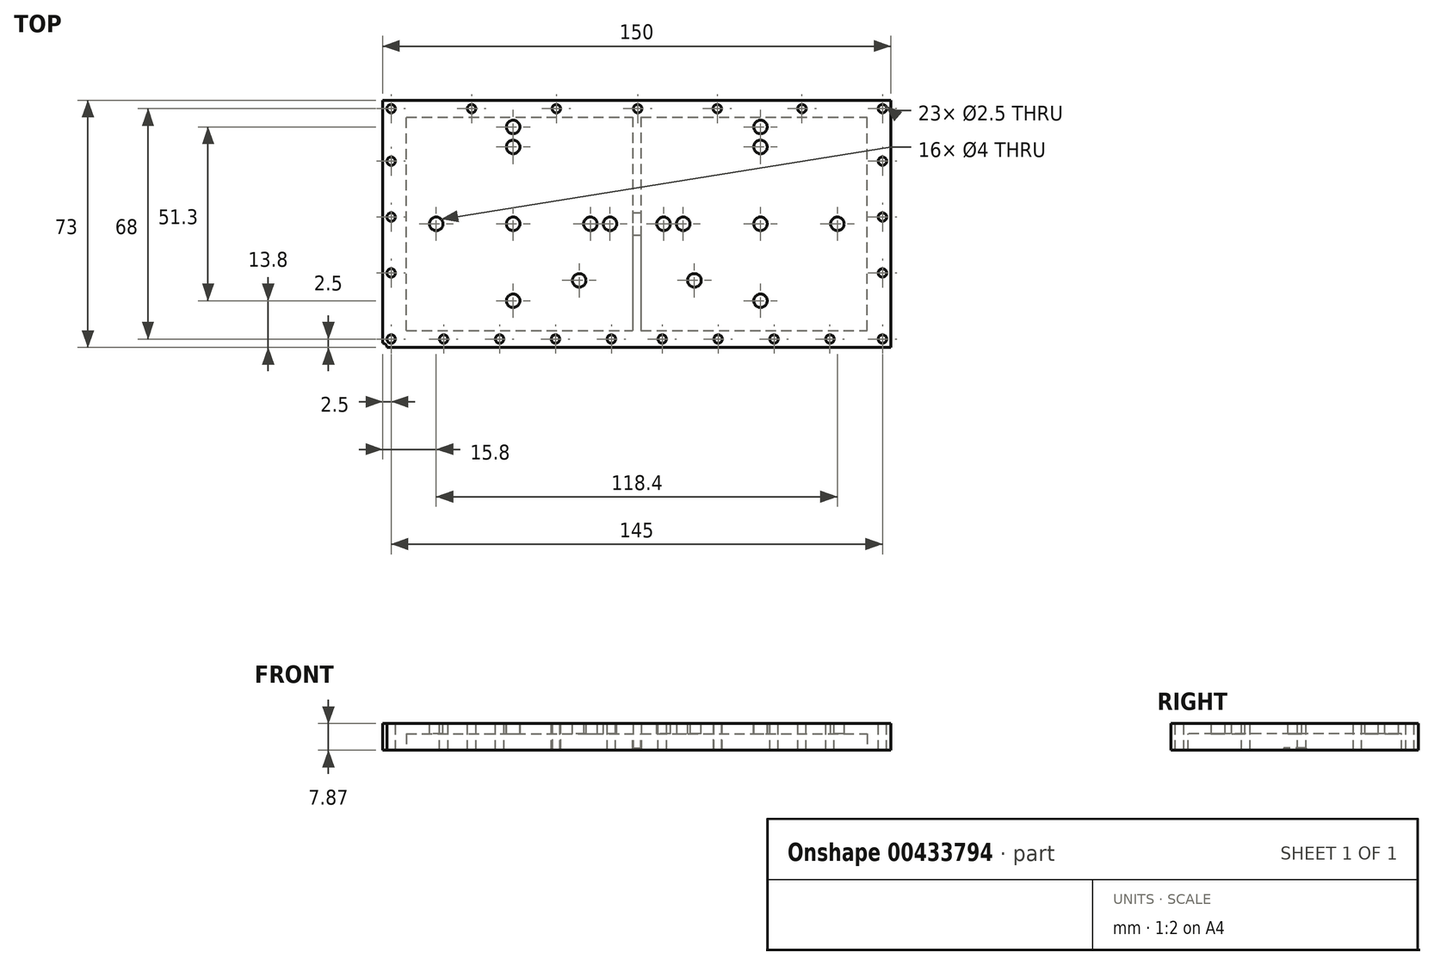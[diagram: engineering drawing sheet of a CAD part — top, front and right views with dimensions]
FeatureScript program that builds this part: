
annotation { "Feature Type Name" : "Feature", "Feature Type Description" : "" }
export const myFeature = defineFeature(function(context is Context, id is Id, definition is map)
    precondition{}
    {
        {
            var Q0;
            Q0=qCreatedBy(makeId("Top.planeOp"),FACE);
            var sketch = newSketch(context, id + "F0", { "sketchPlane" : qUnion([Q0])});
            skLineSegment(sketch, "E0.bottom", {"start": v(0, 0) * mm, "end": v(150, 0) * mm});
            skLineSegment(sketch, "E0.top", {"start": v(0, 73) * mm, "end": v(150, 73) * mm});
            skLineSegment(sketch, "E0.left", {"start": v(0, 0) * mm, "end": v(0, 73) * mm});
            skLineSegment(sketch, "E0.right", {"start": v(150, 0) * mm, "end": v(150, 73) * mm});
            skSolve(sketch);
        }
        {
            var Q0;
            Q0=qSketchRegion(id+"F0",true);
            extrude(context, id + "F1", {"entities" : qUnion([Q0]), "depth" : 7.87 * mm});
        }
        {
            var Q0;
            Q0=qCreatedBy(makeId("Top.planeOp"),FACE);
            var sketch = newSketch(context, id + "F2", { "sketchPlane" : qUnion([Q0])});
            skLineSegment(sketch, "E1.bottom", {"start": v(7, 5) * mm, "end": v(143, 5) * mm});
            skLineSegment(sketch, "E1.top", {"start": v(7, 68) * mm, "end": v(143, 68) * mm});
            skLineSegment(sketch, "E1.left", {"start": v(7, 5) * mm, "end": v(7, 68) * mm});
            skLineSegment(sketch, "E1.right", {"start": v(143, 5) * mm, "end": v(143, 68) * mm});
            skSolve(sketch);
        }
        {
            var Q0;
            Q0=qSketchRegion(id+"F2",true);
            extrude(context, id + "F3", {"entities" : qUnion([Q0]), "operationType" : NewBodyOperationType.REMOVE, "depth" : 4.87 * mm});
        }
        {
            var Q0;
            Q0=makeQuery(id+"F1.opExtrude","CAP_FACE",FACE,{"disambiguationData":[OSD([sQuery(id+"F0.wireOp",EDGE,"E0.bottom"),sQuery(id+"F0.wireOp",EDGE,"E0.top"),sQuery(id+"F0.wireOp",EDGE,"E0.left"),sQuery(id+"F0.wireOp",EDGE,"E0.right")])],"isStart":false});
            var sketch = newSketch(context, id + "F4", { "sketchPlane" : qUnion([Q0])});
            skCircle(sketch, "E2", {"center": v(2.5, 2.5) * mm, "radius": 1.25 * mm});
            skSolve(sketch);
        }
        {
            var Q0;
            Q0=qSketchRegion(id+"F4",true);
            extrude(context, id + "F5", {"entities" : qUnion([Q0]), "operationType" : NewBodyOperationType.REMOVE, "oppositeDirection" : true, "depth" : 7.87 * mm});
        }
        {
            var Q0;
            Q0=makeQuery(id+"F1.opExtrude","CAP_FACE",FACE,{"disambiguationData":[OSD([sQuery(id+"F0.wireOp",EDGE,"E0.bottom"),sQuery(id+"F0.wireOp",EDGE,"E0.top"),sQuery(id+"F0.wireOp",EDGE,"E0.left"),sQuery(id+"F0.wireOp",EDGE,"E0.right")])],"isStart":false});
            var sketch = newSketch(context, id + "F6", { "sketchPlane" : qUnion([Q0])});
            skCircle(sketch, "E3", {"center": v(18, 2.5) * mm, "radius": 1.25 * mm});
            skSolve(sketch);
        }
        {
            var Q0;
            Q0=qSketchRegion(id+"F6",true);
            extrude(context, id + "F7", {"entities" : qUnion([Q0]), "operationType" : NewBodyOperationType.REMOVE, "oppositeDirection" : true, "depth" : 7.87 * mm});
        }
        {
            var Q0;
            Q0=makeQuery(id+"F1.opExtrude","CAP_FACE",FACE,{"disambiguationData":[OSD([sQuery(id+"F0.wireOp",EDGE,"E0.bottom"),sQuery(id+"F0.wireOp",EDGE,"E0.top"),sQuery(id+"F0.wireOp",EDGE,"E0.left"),sQuery(id+"F0.wireOp",EDGE,"E0.right")])],"isStart":false});
            var sketch = newSketch(context, id + "F8", { "sketchPlane" : qUnion([Q0])});
            skCircle(sketch, "E4", {"center": v(34.5, 2.5) * mm, "radius": 1.25 * mm});
            skSolve(sketch);
        }
        {
            var Q0;
            Q0=qSketchRegion(id+"F8",true);
            extrude(context, id + "F9", {"entities" : qUnion([Q0]), "operationType" : NewBodyOperationType.REMOVE, "oppositeDirection" : true, "depth" : 7.87 * mm});
        }
        {
            var Q0;
            Q0=makeQuery(id+"F1.opExtrude","CAP_FACE",FACE,{"disambiguationData":[OSD([sQuery(id+"F0.wireOp",EDGE,"E0.bottom"),sQuery(id+"F0.wireOp",EDGE,"E0.top"),sQuery(id+"F0.wireOp",EDGE,"E0.left"),sQuery(id+"F0.wireOp",EDGE,"E0.right")])],"isStart":false});
            var sketch = newSketch(context, id + "F10", { "sketchPlane" : qUnion([Q0])});
            skCircle(sketch, "E5", {"center": v(51, 2.5) * mm, "radius": 1.25 * mm});
            skSolve(sketch);
        }
        {
            var Q0;
            Q0=qSketchRegion(id+"F10",true);
            extrude(context, id + "F11", {"entities" : qUnion([Q0]), "operationType" : NewBodyOperationType.REMOVE, "oppositeDirection" : true, "depth" : 7.87 * mm});
        }
        {
            var Q0;
            Q0=makeQuery(id+"F1.opExtrude","CAP_FACE",FACE,{"disambiguationData":[OSD([sQuery(id+"F0.wireOp",EDGE,"E0.bottom"),sQuery(id+"F0.wireOp",EDGE,"E0.top"),sQuery(id+"F0.wireOp",EDGE,"E0.left"),sQuery(id+"F0.wireOp",EDGE,"E0.right")])],"isStart":false});
            var sketch = newSketch(context, id + "F12", { "sketchPlane" : qUnion([Q0])});
            skCircle(sketch, "E6", {"center": v(67.5, 2.5) * mm, "radius": 1.25 * mm});
            skSolve(sketch);
        }
        {
            var Q0;
            Q0=qSketchRegion(id+"F12",true);
            extrude(context, id + "F13", {"entities" : qUnion([Q0]), "operationType" : NewBodyOperationType.REMOVE, "oppositeDirection" : true, "depth" : 7.87 * mm});
        }
        {
            var Q0;
            Q0=makeQuery(id+"F1.opExtrude","CAP_FACE",FACE,{"disambiguationData":[OSD([sQuery(id+"F0.wireOp",EDGE,"E0.bottom"),sQuery(id+"F0.wireOp",EDGE,"E0.top"),sQuery(id+"F0.wireOp",EDGE,"E0.left"),sQuery(id+"F0.wireOp",EDGE,"E0.right")])],"isStart":false});
            var sketch = newSketch(context, id + "F14", { "sketchPlane" : qUnion([Q0])});
            skCircle(sketch, "E7", {"center": v(82.5, 2.5) * mm, "radius": 1.25 * mm});
            skSolve(sketch);
        }
        {
            var Q0;
            Q0=qSketchRegion(id+"F14",true);
            extrude(context, id + "F15", {"entities" : qUnion([Q0]), "operationType" : NewBodyOperationType.REMOVE, "oppositeDirection" : true, "depth" : 7.87 * mm});
        }
        {
            var Q0;
            Q0=makeQuery(id+"F1.opExtrude","CAP_FACE",FACE,{"disambiguationData":[OSD([sQuery(id+"F0.wireOp",EDGE,"E0.bottom"),sQuery(id+"F0.wireOp",EDGE,"E0.top"),sQuery(id+"F0.wireOp",EDGE,"E0.left"),sQuery(id+"F0.wireOp",EDGE,"E0.right")])],"isStart":false});
            var sketch = newSketch(context, id + "F16", { "sketchPlane" : qUnion([Q0])});
            skCircle(sketch, "E8", {"center": v(99, 2.5) * mm, "radius": 1.25 * mm});
            skSolve(sketch);
        }
        {
            var Q0;
            Q0=qSketchRegion(id+"F16",true);
            extrude(context, id + "F17", {"entities" : qUnion([Q0]), "operationType" : NewBodyOperationType.REMOVE, "oppositeDirection" : true, "depth" : 7.87 * mm});
        }
        {
            var Q0;
            Q0=makeQuery(id+"F1.opExtrude","CAP_FACE",FACE,{"disambiguationData":[OSD([sQuery(id+"F0.wireOp",EDGE,"E0.bottom"),sQuery(id+"F0.wireOp",EDGE,"E0.top"),sQuery(id+"F0.wireOp",EDGE,"E0.left"),sQuery(id+"F0.wireOp",EDGE,"E0.right")])],"isStart":false});
            var sketch = newSketch(context, id + "F18", { "sketchPlane" : qUnion([Q0])});
            skCircle(sketch, "E9", {"center": v(115.5, 2.5) * mm, "radius": 1.25 * mm});
            skSolve(sketch);
        }
        {
            var Q0;
            Q0=qSketchRegion(id+"F18",true);
            extrude(context, id + "F19", {"entities" : qUnion([Q0]), "operationType" : NewBodyOperationType.REMOVE, "oppositeDirection" : true, "depth" : 7.87 * mm});
        }
        {
            var Q0;
            Q0=makeQuery(id+"F1.opExtrude","CAP_FACE",FACE,{"disambiguationData":[OSD([sQuery(id+"F0.wireOp",EDGE,"E0.bottom"),sQuery(id+"F0.wireOp",EDGE,"E0.top"),sQuery(id+"F0.wireOp",EDGE,"E0.left"),sQuery(id+"F0.wireOp",EDGE,"E0.right")])],"isStart":false});
            var sketch = newSketch(context, id + "F20", { "sketchPlane" : qUnion([Q0])});
            skCircle(sketch, "E10", {"center": v(132, 2.5) * mm, "radius": 1.25 * mm});
            skSolve(sketch);
        }
        {
            var Q0;
            Q0=qSketchRegion(id+"F20",true);
            extrude(context, id + "F21", {"entities" : qUnion([Q0]), "operationType" : NewBodyOperationType.REMOVE, "oppositeDirection" : true, "depth" : 7.87 * mm});
        }
        {
            var Q0;
            Q0=makeQuery(id+"F1.opExtrude","CAP_FACE",FACE,{"disambiguationData":[OSD([sQuery(id+"F0.wireOp",EDGE,"E0.bottom"),sQuery(id+"F0.wireOp",EDGE,"E0.top"),sQuery(id+"F0.wireOp",EDGE,"E0.left"),sQuery(id+"F0.wireOp",EDGE,"E0.right")])],"isStart":false});
            var sketch = newSketch(context, id + "F22", { "sketchPlane" : qUnion([Q0])});
            skCircle(sketch, "E11", {"center": v(147.5, 2.5) * mm, "radius": 1.25 * mm});
            skSolve(sketch);
        }
        {
            var Q0;
            Q0=qSketchRegion(id+"F22",true);
            extrude(context, id + "F23", {"entities" : qUnion([Q0]), "operationType" : NewBodyOperationType.REMOVE, "oppositeDirection" : true, "depth" : 7.87 * mm});
        }
        {
            var Q0;
            Q0=makeQuery(id+"F1.opExtrude","CAP_FACE",FACE,{"disambiguationData":[OSD([sQuery(id+"F0.wireOp",EDGE,"E0.bottom"),sQuery(id+"F0.wireOp",EDGE,"E0.top"),sQuery(id+"F0.wireOp",EDGE,"E0.left"),sQuery(id+"F0.wireOp",EDGE,"E0.right")])],"isStart":false});
            var sketch = newSketch(context, id + "F24", { "sketchPlane" : qUnion([Q0])});
            skCircle(sketch, "E12", {"center": v(2.5, 22) * mm, "radius": 1.25 * mm});
            skSolve(sketch);
        }
        {
            var Q0;
            Q0=qSketchRegion(id+"F24",true);
            extrude(context, id + "F25", {"entities" : qUnion([Q0]), "operationType" : NewBodyOperationType.REMOVE, "oppositeDirection" : true, "depth" : 7.87 * mm});
        }
        {
            var Q0;
            Q0=makeQuery(id+"F1.opExtrude","CAP_FACE",FACE,{"disambiguationData":[OSD([sQuery(id+"F0.wireOp",EDGE,"E0.bottom"),sQuery(id+"F0.wireOp",EDGE,"E0.top"),sQuery(id+"F0.wireOp",EDGE,"E0.left"),sQuery(id+"F0.wireOp",EDGE,"E0.right")])],"isStart":false});
            var sketch = newSketch(context, id + "F26", { "sketchPlane" : qUnion([Q0])});
            skCircle(sketch, "E13", {"center": v(147.5, 22) * mm, "radius": 1.25 * mm});
            skSolve(sketch);
        }
        {
            var Q0;
            Q0=qSketchRegion(id+"F26",true);
            extrude(context, id + "F27", {"entities" : qUnion([Q0]), "operationType" : NewBodyOperationType.REMOVE, "oppositeDirection" : true, "depth" : 7.87 * mm});
        }
        {
            var Q0;
            Q0=makeQuery(id+"F1.opExtrude","CAP_FACE",FACE,{"disambiguationData":[OSD([sQuery(id+"F0.wireOp",EDGE,"E0.bottom"),sQuery(id+"F0.wireOp",EDGE,"E0.top"),sQuery(id+"F0.wireOp",EDGE,"E0.left"),sQuery(id+"F0.wireOp",EDGE,"E0.right")])],"isStart":false});
            var sketch = newSketch(context, id + "F28", { "sketchPlane" : qUnion([Q0])});
            skCircle(sketch, "E14", {"center": v(147.5, 38.5) * mm, "radius": 1.25 * mm});
            skSolve(sketch);
        }
        {
            var Q0;
            Q0=qSketchRegion(id+"F28",true);
            extrude(context, id + "F29", {"entities" : qUnion([Q0]), "operationType" : NewBodyOperationType.REMOVE, "oppositeDirection" : true, "depth" : 7.87 * mm});
        }
        {
            var Q0;
            Q0=makeQuery(id+"F1.opExtrude","CAP_FACE",FACE,{"disambiguationData":[OSD([sQuery(id+"F0.wireOp",EDGE,"E0.bottom"),sQuery(id+"F0.wireOp",EDGE,"E0.top"),sQuery(id+"F0.wireOp",EDGE,"E0.left"),sQuery(id+"F0.wireOp",EDGE,"E0.right")])],"isStart":false});
            var sketch = newSketch(context, id + "F30", { "sketchPlane" : qUnion([Q0])});
            skCircle(sketch, "E15", {"center": v(2.5, 38.5) * mm, "radius": 1.25 * mm});
            skSolve(sketch);
        }
        {
            var Q0;
            Q0=qSketchRegion(id+"F30",true);
            extrude(context, id + "F31", {"entities" : qUnion([Q0]), "operationType" : NewBodyOperationType.REMOVE, "oppositeDirection" : true, "depth" : 7.87 * mm});
        }
        {
            var Q0;
            Q0=makeQuery(id+"F1.opExtrude","CAP_FACE",FACE,{"disambiguationData":[OSD([sQuery(id+"F0.wireOp",EDGE,"E0.bottom"),sQuery(id+"F0.wireOp",EDGE,"E0.top"),sQuery(id+"F0.wireOp",EDGE,"E0.left"),sQuery(id+"F0.wireOp",EDGE,"E0.right")])],"isStart":false});
            var sketch = newSketch(context, id + "F32", { "sketchPlane" : qUnion([Q0])});
            skCircle(sketch, "E16", {"center": v(2.5, 55) * mm, "radius": 1.25 * mm});
            skSolve(sketch);
        }
        {
            var Q0;
            Q0=qSketchRegion(id+"F32",true);
            extrude(context, id + "F33", {"entities" : qUnion([Q0]), "operationType" : NewBodyOperationType.REMOVE, "oppositeDirection" : true, "depth" : 7.87 * mm});
        }
        {
            var Q0;
            Q0=makeQuery(id+"F1.opExtrude","CAP_FACE",FACE,{"disambiguationData":[OSD([sQuery(id+"F0.wireOp",EDGE,"E0.bottom"),sQuery(id+"F0.wireOp",EDGE,"E0.top"),sQuery(id+"F0.wireOp",EDGE,"E0.left"),sQuery(id+"F0.wireOp",EDGE,"E0.right")])],"isStart":false});
            var sketch = newSketch(context, id + "F34", { "sketchPlane" : qUnion([Q0])});
            skCircle(sketch, "E17", {"center": v(147.5, 55) * mm, "radius": 1.25 * mm});
            skSolve(sketch);
        }
        {
            var Q0;
            Q0=qSketchRegion(id+"F34",true);
            extrude(context, id + "F35", {"entities" : qUnion([Q0]), "operationType" : NewBodyOperationType.REMOVE, "oppositeDirection" : true, "depth" : 7.87 * mm});
        }
        {
            var Q0;
            Q0=makeQuery(id+"F1.opExtrude","CAP_FACE",FACE,{"disambiguationData":[OSD([sQuery(id+"F0.wireOp",EDGE,"E0.bottom"),sQuery(id+"F0.wireOp",EDGE,"E0.top"),sQuery(id+"F0.wireOp",EDGE,"E0.left"),sQuery(id+"F0.wireOp",EDGE,"E0.right")])],"isStart":false});
            var sketch = newSketch(context, id + "F36", { "sketchPlane" : qUnion([Q0])});
            skCircle(sketch, "E18", {"center": v(2.5, 70.5) * mm, "radius": 1.25 * mm});
            skSolve(sketch);
        }
        {
            var Q0;
            Q0=qSketchRegion(id+"F36",true);
            extrude(context, id + "F37", {"entities" : qUnion([Q0]), "operationType" : NewBodyOperationType.REMOVE, "oppositeDirection" : true, "depth" : 7.87 * mm});
        }
        {
            var Q0;
            Q0=makeQuery(id+"F1.opExtrude","CAP_FACE",FACE,{"disambiguationData":[OSD([sQuery(id+"F0.wireOp",EDGE,"E0.bottom"),sQuery(id+"F0.wireOp",EDGE,"E0.top"),sQuery(id+"F0.wireOp",EDGE,"E0.left"),sQuery(id+"F0.wireOp",EDGE,"E0.right")])],"isStart":false});
            var sketch = newSketch(context, id + "F38", { "sketchPlane" : qUnion([Q0])});
            skCircle(sketch, "E19", {"center": v(147.5, 70.5) * mm, "radius": 1.25 * mm});
            skSolve(sketch);
        }
        {
            var Q0;
            Q0=qSketchRegion(id+"F38",true);
            extrude(context, id + "F39", {"entities" : qUnion([Q0]), "operationType" : NewBodyOperationType.REMOVE, "oppositeDirection" : true, "depth" : 7.87 * mm});
        }
        {
            var Q0;
            Q0=makeQuery(id+"F1.opExtrude","CAP_FACE",FACE,{"disambiguationData":[OSD([sQuery(id+"F0.wireOp",EDGE,"E0.bottom"),sQuery(id+"F0.wireOp",EDGE,"E0.top"),sQuery(id+"F0.wireOp",EDGE,"E0.left"),sQuery(id+"F0.wireOp",EDGE,"E0.right")])],"isStart":false});
            var sketch = newSketch(context, id + "F40", { "sketchPlane" : qUnion([Q0])});
            skCircle(sketch, "E20", {"center": v(26.25, 70.5) * mm, "radius": 1.25 * mm});
            skCircle(sketch, "E21", {"center": v(0, 0) * mm, "radius": 1.25 * mm});
            skSolve(sketch);
        }
        {
            var Q0;
            Q0=qSketchRegion(id+"F40",true);
            extrude(context, id + "F41", {"entities" : qUnion([Q0]), "operationType" : NewBodyOperationType.REMOVE, "oppositeDirection" : true, "depth" : 7.87 * mm});
        }
        {
            var Q0;
            Q0=makeQuery(id+"F1.opExtrude","CAP_FACE",FACE,{"disambiguationData":[OSD([sQuery(id+"F0.wireOp",EDGE,"E0.bottom"),sQuery(id+"F0.wireOp",EDGE,"E0.top"),sQuery(id+"F0.wireOp",EDGE,"E0.left"),sQuery(id+"F0.wireOp",EDGE,"E0.right")])],"isStart":false});
            var sketch = newSketch(context, id + "F42", { "sketchPlane" : qUnion([Q0])});
            skCircle(sketch, "E22", {"center": v(123.75, 70.5) * mm, "radius": 1.25 * mm});
            skSolve(sketch);
        }
        {
            var Q0;
            Q0=qSketchRegion(id+"F42",true);
            extrude(context, id + "F43", {"entities" : qUnion([Q0]), "operationType" : NewBodyOperationType.REMOVE, "oppositeDirection" : true, "depth" : 7.87 * mm});
        }
        {
            var Q0;
            Q0=makeQuery(id+"F1.opExtrude","CAP_FACE",FACE,{"disambiguationData":[OSD([sQuery(id+"F0.wireOp",EDGE,"E0.bottom"),sQuery(id+"F0.wireOp",EDGE,"E0.top"),sQuery(id+"F0.wireOp",EDGE,"E0.left"),sQuery(id+"F0.wireOp",EDGE,"E0.right")])],"isStart":false});
            var sketch = newSketch(context, id + "F44", { "sketchPlane" : qUnion([Q0])});
            skCircle(sketch, "E23", {"center": v(75.25, 70.5) * mm, "radius": 1.25 * mm});
            skSolve(sketch);
        }
        {
            var Q0;
            Q0=qSketchRegion(id+"F44",true);
            extrude(context, id + "F45", {"entities" : qUnion([Q0]), "operationType" : NewBodyOperationType.REMOVE, "oppositeDirection" : true, "depth" : 7.87 * mm});
        }
        {
            var Q0;
            Q0=makeQuery(id+"F1.opExtrude","CAP_FACE",FACE,{"disambiguationData":[OSD([sQuery(id+"F0.wireOp",EDGE,"E0.bottom"),sQuery(id+"F0.wireOp",EDGE,"E0.top"),sQuery(id+"F0.wireOp",EDGE,"E0.left"),sQuery(id+"F0.wireOp",EDGE,"E0.right")])],"isStart":false});
            var sketch = newSketch(context, id + "F46", { "sketchPlane" : qUnion([Q0])});
            skCircle(sketch, "E24", {"center": v(38.5, 65.1) * mm, "radius": 2 * mm});
            skSolve(sketch);
        }
        {
            var Q0;
            Q0=qSketchRegion(id+"F46",true);
            extrude(context, id + "F47", {"entities" : qUnion([Q0]), "operationType" : NewBodyOperationType.REMOVE, "oppositeDirection" : true, "depth" : 3 * mm});
        }
        {
            var Q0;
            Q0=makeQuery(id+"F1.opExtrude","CAP_FACE",FACE,{"disambiguationData":[OSD([sQuery(id+"F0.wireOp",EDGE,"E0.bottom"),sQuery(id+"F0.wireOp",EDGE,"E0.top"),sQuery(id+"F0.wireOp",EDGE,"E0.left"),sQuery(id+"F0.wireOp",EDGE,"E0.right")])],"isStart":false});
            var sketch = newSketch(context, id + "F48", { "sketchPlane" : qUnion([Q0])});
            skCircle(sketch, "E25", {"center": v(38.5, 59.2) * mm, "radius": 2 * mm});
            skSolve(sketch);
        }
        {
            var Q0;
            Q0=qSketchRegion(id+"F48",true);
            extrude(context, id + "F49", {"entities" : qUnion([Q0]), "operationType" : NewBodyOperationType.REMOVE, "oppositeDirection" : true, "depth" : 3 * mm});
        }
        {
            var Q0;
            Q0=makeQuery(id+"F1.opExtrude","CAP_FACE",FACE,{"disambiguationData":[OSD([sQuery(id+"F0.wireOp",EDGE,"E0.bottom"),sQuery(id+"F0.wireOp",EDGE,"E0.top"),sQuery(id+"F0.wireOp",EDGE,"E0.left"),sQuery(id+"F0.wireOp",EDGE,"E0.right")])],"isStart":false});
            var sketch = newSketch(context, id + "F50", { "sketchPlane" : qUnion([Q0])});
            skCircle(sketch, "E26", {"center": v(15.8, 36.5) * mm, "radius": 2 * mm});
            skSolve(sketch);
        }
        {
            var Q0;
            Q0=qSketchRegion(id+"F50",true);
            extrude(context, id + "F51", {"entities" : qUnion([Q0]), "operationType" : NewBodyOperationType.REMOVE, "oppositeDirection" : true, "depth" : 3 * mm});
        }
        {
            var Q0;
            Q0=makeQuery(id+"F1.opExtrude","CAP_FACE",FACE,{"disambiguationData":[OSD([sQuery(id+"F0.wireOp",EDGE,"E0.bottom"),sQuery(id+"F0.wireOp",EDGE,"E0.top"),sQuery(id+"F0.wireOp",EDGE,"E0.left"),sQuery(id+"F0.wireOp",EDGE,"E0.right")])],"isStart":false});
            var sketch = newSketch(context, id + "F52", { "sketchPlane" : qUnion([Q0])});
            skCircle(sketch, "E27", {"center": v(67.1, 36.5) * mm, "radius": 2 * mm});
            skSolve(sketch);
        }
        {
            var Q0;
            Q0=qSketchRegion(id+"F52",true);
            extrude(context, id + "F53", {"entities" : qUnion([Q0]), "operationType" : NewBodyOperationType.REMOVE, "oppositeDirection" : true, "depth" : 3 * mm});
        }
        {
            var Q0;
            Q0=makeQuery(id+"F1.opExtrude","CAP_FACE",FACE,{"disambiguationData":[OSD([sQuery(id+"F0.wireOp",EDGE,"E0.bottom"),sQuery(id+"F0.wireOp",EDGE,"E0.top"),sQuery(id+"F0.wireOp",EDGE,"E0.left"),sQuery(id+"F0.wireOp",EDGE,"E0.right")])],"isStart":false});
            var sketch = newSketch(context, id + "F54", { "sketchPlane" : qUnion([Q0])});
            skCircle(sketch, "E28", {"center": v(111.5, 65.1) * mm, "radius": 2 * mm});
            skSolve(sketch);
        }
        {
            var Q0;
            Q0=qSketchRegion(id+"F54",true);
            extrude(context, id + "F55", {"entities" : qUnion([Q0]), "operationType" : NewBodyOperationType.REMOVE, "oppositeDirection" : true, "depth" : 3 * mm});
        }
        {
            var Q0;
            Q0=makeQuery(id+"F1.opExtrude","CAP_FACE",FACE,{"disambiguationData":[OSD([sQuery(id+"F0.wireOp",EDGE,"E0.bottom"),sQuery(id+"F0.wireOp",EDGE,"E0.top"),sQuery(id+"F0.wireOp",EDGE,"E0.left"),sQuery(id+"F0.wireOp",EDGE,"E0.right")])],"isStart":false});
            var sketch = newSketch(context, id + "F56", { "sketchPlane" : qUnion([Q0])});
            skCircle(sketch, "E29", {"center": v(111.5, 59.2) * mm, "radius": 2 * mm});
            skSolve(sketch);
        }
        {
            var Q0;
            Q0=qSketchRegion(id+"F56",true);
            extrude(context, id + "F57", {"entities" : qUnion([Q0]), "operationType" : NewBodyOperationType.REMOVE, "oppositeDirection" : true, "depth" : 3 * mm});
        }
        {
            var Q0;
            Q0=makeQuery(id+"F1.opExtrude","CAP_FACE",FACE,{"disambiguationData":[OSD([sQuery(id+"F0.wireOp",EDGE,"E0.bottom"),sQuery(id+"F0.wireOp",EDGE,"E0.top"),sQuery(id+"F0.wireOp",EDGE,"E0.left"),sQuery(id+"F0.wireOp",EDGE,"E0.right")])],"isStart":false});
            var sketch = newSketch(context, id + "F58", { "sketchPlane" : qUnion([Q0])});
            skCircle(sketch, "E30", {"center": v(82.9, 36.5) * mm, "radius": 2 * mm});
            skSolve(sketch);
        }
        {
            var Q0;
            Q0=qSketchRegion(id+"F58",true);
            extrude(context, id + "F59", {"entities" : qUnion([Q0]), "operationType" : NewBodyOperationType.REMOVE, "oppositeDirection" : true, "depth" : 3 * mm});
        }
        {
            var Q0;
            Q0=makeQuery(id+"F1.opExtrude","CAP_FACE",FACE,{"disambiguationData":[OSD([sQuery(id+"F0.wireOp",EDGE,"E0.bottom"),sQuery(id+"F0.wireOp",EDGE,"E0.top"),sQuery(id+"F0.wireOp",EDGE,"E0.left"),sQuery(id+"F0.wireOp",EDGE,"E0.right")])],"isStart":false});
            var sketch = newSketch(context, id + "F60", { "sketchPlane" : qUnion([Q0])});
            skCircle(sketch, "E31", {"center": v(134.2, 36.5) * mm, "radius": 2 * mm});
            skSolve(sketch);
        }
        {
            var Q0;
            Q0=qSketchRegion(id+"F60",true);
            extrude(context, id + "F61", {"entities" : qUnion([Q0]), "operationType" : NewBodyOperationType.REMOVE, "oppositeDirection" : true, "depth" : 3 * mm});
        }
        {
            var Q0;
            Q0=makeQuery(id+"F1.opExtrude","CAP_FACE",FACE,{"disambiguationData":[OSD([sQuery(id+"F0.wireOp",EDGE,"E0.bottom"),sQuery(id+"F0.wireOp",EDGE,"E0.top"),sQuery(id+"F0.wireOp",EDGE,"E0.left"),sQuery(id+"F0.wireOp",EDGE,"E0.right")])],"isStart":false});
            var sketch = newSketch(context, id + "F62", { "sketchPlane" : qUnion([Q0])});
            skCircle(sketch, "E32", {"center": v(58, 19.8) * mm, "radius": 2 * mm});
            skSolve(sketch);
        }
        {
            var Q0;
            Q0=qSketchRegion(id+"F62",true);
            extrude(context, id + "F63", {"entities" : qUnion([Q0]), "operationType" : NewBodyOperationType.REMOVE, "oppositeDirection" : true, "depth" : 3 * mm});
        }
        {
            var Q0;
            Q0=makeQuery(id+"F1.opExtrude","CAP_FACE",FACE,{"disambiguationData":[OSD([sQuery(id+"F0.wireOp",EDGE,"E0.bottom"),sQuery(id+"F0.wireOp",EDGE,"E0.top"),sQuery(id+"F0.wireOp",EDGE,"E0.left"),sQuery(id+"F0.wireOp",EDGE,"E0.right")])],"isStart":false});
            var sketch = newSketch(context, id + "F64", { "sketchPlane" : qUnion([Q0])});
            skCircle(sketch, "E33", {"center": v(92, 19.8) * mm, "radius": 2 * mm});
            skSolve(sketch);
        }
        {
            var Q0;
            Q0=qSketchRegion(id+"F64",true);
            extrude(context, id + "F65", {"entities" : qUnion([Q0]), "operationType" : NewBodyOperationType.REMOVE, "oppositeDirection" : true, "depth" : 3 * mm});
        }
        {
            var Q0;
            Q0=makeQuery(id+"F3.boolean.opBoolean","COPY",FACE,{"derivedFrom":makeQuery(id+"F3.opExtrude","SWEPT_FACE",FACE,{"disambiguationData":[OSD([sQuery(id+"F2.wireOp",EDGE,"E1.bottom")])]})});
            var sketch = newSketch(context, id + "F66", { "sketchPlane" : qUnion([Q0])});
            skLineSegment(sketch, "E34.bottom", {"start": v(-73.75, 0) * mm, "end": v(-76.25, 0) * mm});
            skLineSegment(sketch, "E34.top", {"start": v(-73.75, 4.87) * mm, "end": v(-76.25, 4.87) * mm});
            skLineSegment(sketch, "E34.left", {"start": v(-73.75, 0) * mm, "end": v(-73.75, 4.87) * mm});
            skLineSegment(sketch, "E34.right", {"start": v(-76.25, 0) * mm, "end": v(-76.25, 4.87) * mm});
            skSolve(sketch);
        }
        {
            var Q0;
            Q0=makeQuery(id+"F66.imprint","IMPRINT",FACE,{"disambiguationData":[TD([[makeQuery(id+"F66.imprint","IMPRINT",EDGE,{"derivedFrom":sQuery(id+"F66.wireOp",EDGE,"E34.bottom")}),-1.0]])]});
            extrude(context, id + "F67", {"entities" : qUnion([Q0]), "operationType" : NewBodyOperationType.ADD, "depth" : 63 * mm});
        }
        {
            var Q0;
            Q0=makeQuery(id+"F67.boolean.opBoolean","MERGE",FACE,{"derivedFrom":[makeQuery(id+"F1.opExtrude","CAP_FACE",FACE,{"disambiguationData":[OSD([sQuery(id+"F0.wireOp",EDGE,"E0.bottom"),sQuery(id+"F0.wireOp",EDGE,"E0.top"),sQuery(id+"F0.wireOp",EDGE,"E0.left"),sQuery(id+"F0.wireOp",EDGE,"E0.right")])],"isStart":true}),makeQuery(id+"F67.opExtrude","SWEPT_FACE",FACE,{"disambiguationData":[OSD([sQuery(id+"F66.wireOp",EDGE,"E34.bottom")])]})]});
            var sketch = newSketch(context, id + "F68", { "sketchPlane" : qUnion([Q0])});
            skLineSegment(sketch, "E35.bottom", {"start": v(73.75, -33.25) * mm, "end": v(76.25, -33.25) * mm});
            skLineSegment(sketch, "E35.top", {"start": v(73.75, -39.75) * mm, "end": v(76.25, -39.75) * mm});
            skLineSegment(sketch, "E35.left", {"start": v(73.75, -33.25) * mm, "end": v(73.75, -39.75) * mm});
            skLineSegment(sketch, "E35.right", {"start": v(76.25, -33.25) * mm, "end": v(76.25, -39.75) * mm});
            skSolve(sketch);
        }
        {
            var Q0;
            Q0=qSketchRegion(id+"F68",true);
            extrude(context, id + "F69", {"entities" : qUnion([Q0]), "operationType" : NewBodyOperationType.REMOVE, "oppositeDirection" : true, "depth" : 0.62 * mm});
        }
        {
            var Q0;
            {var subQ0=sQuery(id+"F2.wireOp",EDGE,"E1.top");var subQ1=sQuery(id+"F2.wireOp",EDGE,"E1.bottom");var subQ2=sQuery(id+"F2.wireOp",EDGE,"E1.left");Q0=makeQuery(id+"F67.boolean.opBoolean","SPLIT",FACE,{"disambiguationData":[TD([makeQuery(id+"F3.boolean.opBoolean","COPY",FACE,{"derivedFrom":makeQuery(id+"F3.opExtrude","SWEPT_FACE",FACE,{"disambiguationData":[OSD([subQ2])]})})])],"derivedFrom":makeQuery(id+"F3.boolean.opBoolean","COPY",FACE,{"derivedFrom":makeQuery(id+"F3.opExtrude","CAP_FACE",FACE,{"disambiguationData":[OSD([subQ1,subQ0,subQ2,sQuery(id+"F2.wireOp",EDGE,"E1.right")])],"isStart":false})})});}
            var sketch = newSketch(context, id + "F70", { "sketchPlane" : qUnion([Q0])});
            skCircle(sketch, "E36", {"center": v(38.5, -13.8) * mm, "radius": 2 * mm});
            skSolve(sketch);
        }
        {
            var Q0;
            Q0=qSketchRegion(id+"F70",true);
            extrude(context, id + "F71", {"entities" : qUnion([Q0]), "operationType" : NewBodyOperationType.REMOVE, "oppositeDirection" : true, "depth" : 3 * mm});
        }
        {
            var Q0;
            {var subQ0=sQuery(id+"F2.wireOp",EDGE,"E1.left");var subQ1=sQuery(id+"F2.wireOp",EDGE,"E1.top");var subQ2=sQuery(id+"F2.wireOp",EDGE,"E1.bottom");Q0=makeQuery(id+"F67.boolean.opBoolean","SPLIT",FACE,{"disambiguationData":[TD([makeQuery(id+"F3.boolean.opBoolean","COPY",FACE,{"derivedFrom":makeQuery(id+"F3.opExtrude","SWEPT_FACE",FACE,{"disambiguationData":[OSD([subQ0])]})})])],"derivedFrom":makeQuery(id+"F3.boolean.opBoolean","COPY",FACE,{"derivedFrom":makeQuery(id+"F3.opExtrude","CAP_FACE",FACE,{"disambiguationData":[OSD([subQ2,subQ1,subQ0,sQuery(id+"F2.wireOp",EDGE,"E1.right")])],"isStart":false})})});}
            var sketch = newSketch(context, id + "F72", { "sketchPlane" : qUnion([Q0])});
            skCircle(sketch, "E37", {"center": v(38.5, -36.5) * mm, "radius": 2 * mm});
            skSolve(sketch);
        }
        {
            var Q0;
            {var subQ0=sQuery(id+"F2.wireOp",EDGE,"E1.right");var subQ1=sQuery(id+"F2.wireOp",EDGE,"E1.top");var subQ2=sQuery(id+"F2.wireOp",EDGE,"E1.bottom");Q0=makeQuery(id+"F67.boolean.opBoolean","SPLIT",FACE,{"disambiguationData":[TD([makeQuery(id+"F3.boolean.opBoolean","COPY",FACE,{"derivedFrom":makeQuery(id+"F3.opExtrude","SWEPT_FACE",FACE,{"disambiguationData":[OSD([subQ0])]})})])],"derivedFrom":makeQuery(id+"F3.boolean.opBoolean","COPY",FACE,{"derivedFrom":makeQuery(id+"F3.opExtrude","CAP_FACE",FACE,{"disambiguationData":[OSD([subQ2,subQ1,sQuery(id+"F2.wireOp",EDGE,"E1.left"),subQ0])],"isStart":false})})});}
            var sketch = newSketch(context, id + "F73", { "sketchPlane" : qUnion([Q0])});
            skCircle(sketch, "E38", {"center": v(111.5, -36.5) * mm, "radius": 2 * mm});
            skSolve(sketch);
        }
        {
            var Q0;
            Q0=qSketchRegion(id+"F73",true);
            extrude(context, id + "F74", {"entities" : qUnion([Q0]), "operationType" : NewBodyOperationType.REMOVE, "oppositeDirection" : true, "depth" : 3 * mm});
        }
        {
            var Q0;
            {var subQ0=sQuery(id+"F2.wireOp",EDGE,"E1.right");var subQ1=sQuery(id+"F2.wireOp",EDGE,"E1.top");var subQ2=sQuery(id+"F2.wireOp",EDGE,"E1.bottom");Q0=makeQuery(id+"F67.boolean.opBoolean","SPLIT",FACE,{"disambiguationData":[TD([makeQuery(id+"F3.boolean.opBoolean","COPY",FACE,{"derivedFrom":makeQuery(id+"F3.opExtrude","SWEPT_FACE",FACE,{"disambiguationData":[OSD([subQ0])]})})])],"derivedFrom":makeQuery(id+"F3.boolean.opBoolean","COPY",FACE,{"derivedFrom":makeQuery(id+"F3.opExtrude","CAP_FACE",FACE,{"disambiguationData":[OSD([subQ2,subQ1,sQuery(id+"F2.wireOp",EDGE,"E1.left"),subQ0])],"isStart":false})})});}
            var sketch = newSketch(context, id + "F75", { "sketchPlane" : qUnion([Q0])});
            skCircle(sketch, "E39", {"center": v(111.5, -13.8) * mm, "radius": 2 * mm});
            skSolve(sketch);
        }
        {
            var Q0;
            Q0=qSketchRegion(id+"F75",true);
            extrude(context, id + "F76", {"entities" : qUnion([Q0]), "operationType" : NewBodyOperationType.REMOVE, "oppositeDirection" : true, "depth" : 3 * mm});
        }
        {
            var Q0;
            {var subQ0=sQuery(id+"F2.wireOp",EDGE,"E1.left");var subQ1=sQuery(id+"F2.wireOp",EDGE,"E1.top");var subQ2=sQuery(id+"F2.wireOp",EDGE,"E1.bottom");Q0=makeQuery(id+"F67.boolean.opBoolean","SPLIT",FACE,{"disambiguationData":[TD([makeQuery(id+"F3.boolean.opBoolean","COPY",FACE,{"derivedFrom":makeQuery(id+"F3.opExtrude","SWEPT_FACE",FACE,{"disambiguationData":[OSD([subQ0])]})})])],"derivedFrom":makeQuery(id+"F3.boolean.opBoolean","COPY",FACE,{"derivedFrom":makeQuery(id+"F3.opExtrude","CAP_FACE",FACE,{"disambiguationData":[OSD([subQ2,subQ1,subQ0,sQuery(id+"F2.wireOp",EDGE,"E1.right")])],"isStart":false})})});}
            var sketch = newSketch(context, id + "F77", { "sketchPlane" : qUnion([Q0])});
            skCircle(sketch, "E40", {"center": v(61.3, -36.5) * mm, "radius": 2 * mm});
            skSolve(sketch);
        }
        {
            var Q0;
            Q0=qSketchRegion(id+"F77",true);
            extrude(context, id + "F78", {"entities" : qUnion([Q0]), "operationType" : NewBodyOperationType.REMOVE, "oppositeDirection" : true, "depth" : 3 * mm});
        }
        {
            var Q0;
            {var subQ0=sQuery(id+"F2.wireOp",EDGE,"E1.right");var subQ1=sQuery(id+"F2.wireOp",EDGE,"E1.top");var subQ2=sQuery(id+"F2.wireOp",EDGE,"E1.bottom");Q0=makeQuery(id+"F67.boolean.opBoolean","SPLIT",FACE,{"disambiguationData":[TD([makeQuery(id+"F3.boolean.opBoolean","COPY",FACE,{"derivedFrom":makeQuery(id+"F3.opExtrude","SWEPT_FACE",FACE,{"disambiguationData":[OSD([subQ0])]})})])],"derivedFrom":makeQuery(id+"F3.boolean.opBoolean","COPY",FACE,{"derivedFrom":makeQuery(id+"F3.opExtrude","CAP_FACE",FACE,{"disambiguationData":[OSD([subQ2,subQ1,sQuery(id+"F2.wireOp",EDGE,"E1.left"),subQ0])],"isStart":false})})});}
            var sketch = newSketch(context, id + "F79", { "sketchPlane" : qUnion([Q0])});
            skCircle(sketch, "E41", {"center": v(88.7, -36.5) * mm, "radius": 2 * mm});
            skSolve(sketch);
        }
        {
            var Q0;
            Q0=qSketchRegion(id+"F79",true);
            extrude(context, id + "F80", {"entities" : qUnion([Q0]), "operationType" : NewBodyOperationType.REMOVE, "oppositeDirection" : true, "depth" : 3 * mm});
        }
        {
            var Q0;
            Q0=qSketchRegion(id+"F72",true);
            extrude(context, id + "F81", {"entities" : qUnion([Q0]), "operationType" : NewBodyOperationType.REMOVE, "oppositeDirection" : true, "depth" : 3 * mm});
        }
        {
            var Q0;
            Q0=makeQuery(id+"F67.boolean.opBoolean","MERGE",FACE,{"derivedFrom":[makeQuery(id+"F1.opExtrude","CAP_FACE",FACE,{"disambiguationData":[OSD([sQuery(id+"F0.wireOp",EDGE,"E0.bottom"),sQuery(id+"F0.wireOp",EDGE,"E0.top"),sQuery(id+"F0.wireOp",EDGE,"E0.left"),sQuery(id+"F0.wireOp",EDGE,"E0.right")])],"isStart":true}),makeQuery(id+"F67.opExtrude","SWEPT_FACE",FACE,{"disambiguationData":[OSD([sQuery(id+"F66.wireOp",EDGE,"E34.bottom")])]})]});
            var sketch = newSketch(context, id + "F82", { "sketchPlane" : qUnion([Q0])});
            skCircle(sketch, "E42", {"center": v(51.25, -70.5) * mm, "radius": 1.25 * mm});
            skSolve(sketch);
        }
        {
            var Q0;
            Q0 = qSketchRegion(id + "F82", true);
            extrude(context, id + "F83", {"entities" : qUnion([Q0]), "operationType" : NewBodyOperationType.REMOVE, "oppositeDirection" : true, "depth" : 7.87 * mm});
        }
        {
            var Q0;
            Q0=makeQuery(id+"F67.boolean.opBoolean","MERGE",FACE,{"derivedFrom":[makeQuery(id+"F1.opExtrude","CAP_FACE",FACE,{"disambiguationData":[OSD([sQuery(id+"F0.wireOp",EDGE,"E0.bottom"),sQuery(id+"F0.wireOp",EDGE,"E0.top"),sQuery(id+"F0.wireOp",EDGE,"E0.left"),sQuery(id+"F0.wireOp",EDGE,"E0.right")])],"isStart":true}),makeQuery(id+"F67.opExtrude","SWEPT_FACE",FACE,{"disambiguationData":[OSD([sQuery(id+"F66.wireOp",EDGE,"E34.bottom")])]})]});
            var sketch = newSketch(context, id + "F84", { "sketchPlane" : qUnion([Q0])});
            skCircle(sketch, "E43", {"center": v(98.75, -70.5) * mm, "radius": 1.25 * mm});
            skSolve(sketch);
        }
        {
            var Q0;
            Q0 = qSketchRegion(id + "F84", true);
            extrude(context, id + "F85", {"entities" : qUnion([Q0]), "operationType" : NewBodyOperationType.REMOVE, "oppositeDirection" : true, "depth" : 7.87 * mm});
        }
    });
